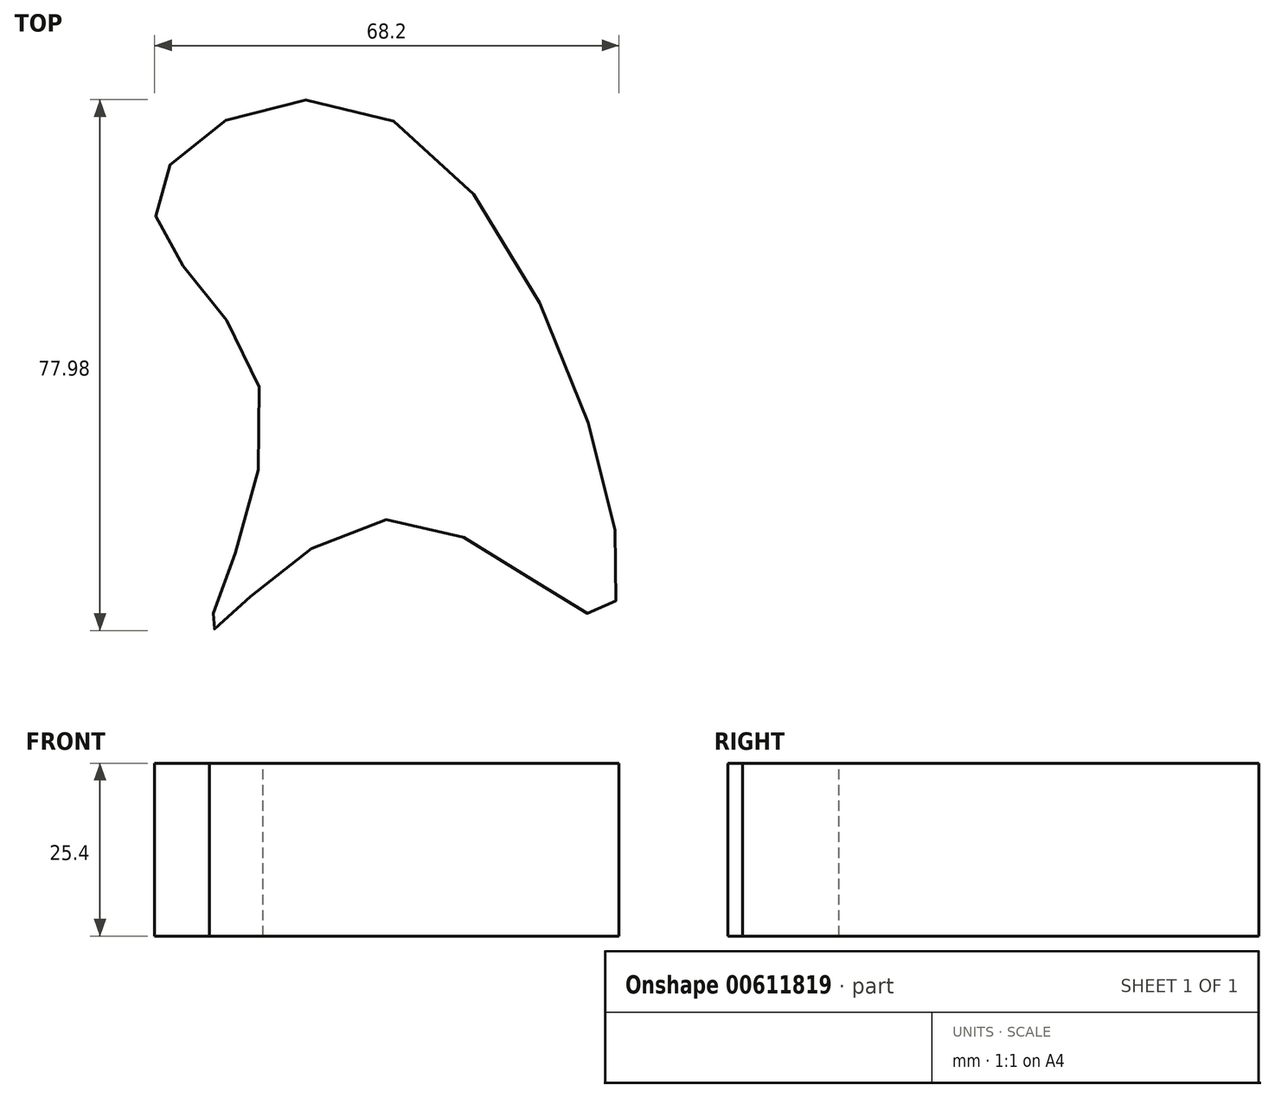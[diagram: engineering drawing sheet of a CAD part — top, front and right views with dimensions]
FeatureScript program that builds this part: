
annotation { "Feature Type Name" : "Feature", "Feature Type Description" : "" }
export const myFeature = defineFeature(function(context is Context, id is Id, definition is map)
    precondition{}
    {
        {
            var Q0;
            Q0=qCreatedBy(makeId("Top.planeOp"),FACE);
            var sketch = newSketch(context, id + "F0", { "sketchPlane" : qUnion([Q0])});
            skFitSpline(sketch, "E0", {"points": [v(0, 40.57) * mm, v(-35.01, 29.09) * mm, v(-19.45, 0) * mm, v(-26.86, -34.27) * mm, v(0, -17.97) * mm, v(31.68, -31.68) * mm, v(0, 40.57) * mm]});
            skSolve(sketch);
        }
        {
            var Q0;
            Q0=sQuery(id+"F0.wireOp",EDGE,"E0");
            extrude(context, id + "F1", {"bodyType" : ToolBodyType.SURFACE, "surfaceEntities" : qUnion([Q0]), "depth" : 25.4 * mm, "offsetDistance" : 25.4 * mm});
        }
    });
